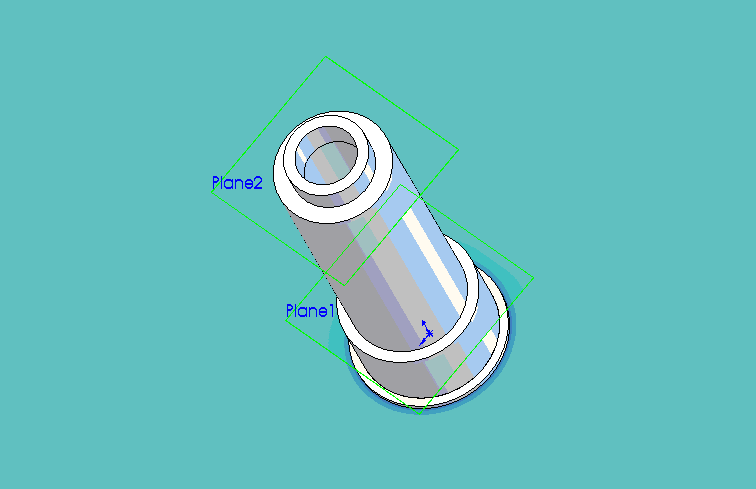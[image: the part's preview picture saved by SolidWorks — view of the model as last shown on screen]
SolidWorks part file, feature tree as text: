
SOLIDWORKS PART (.sldprt)
format: sldprt  version: not decoded by parser v0  size: 94,208 bytes
history: native  units: mm
features: plane x5, sketch x5, extrude x5, material x1 (+10 scaffold rows collapsed)
feature tree (26):
  scaffold x10  (default folders/planes/origin — collapsed)
  material  "Material <not specified>"
  plane  "Frontal"
  plane  "Horizontal"
  plane  "Profile"
  sketch  "Sketch1"  dims[D1=25.0mm]
  extrude  "Extrude1"  Depth=1mm
  sketch  "Sketch2"  dims[D1=~10.516061mm]
  extrude  "Extrude2"  Depth=15mm
  plane  "Plane1"  Offset=14.5mm
  sketch  "Sketch4"  dims[D1=~9.213961mm]
  extrude  "Extrude3"  Depth=55.5mm
  plane  "Plane2"  Offset=54mm
  sketch  "Sketch7"  dims[D1=8.5mm]
  extrude  "Extrude6"  Depth=1.5mm
  sketch  "Sketch8"  dims[D1=~7.282526mm]
  extrude  "Extrude7"  Depth=5mm
decode coverage: 10 of 10 modeling features carry decoded parameters
note: ~ marks probable driven/reference dimensions
note: suppression state not decoded; provenance and decode notes live in map.json
